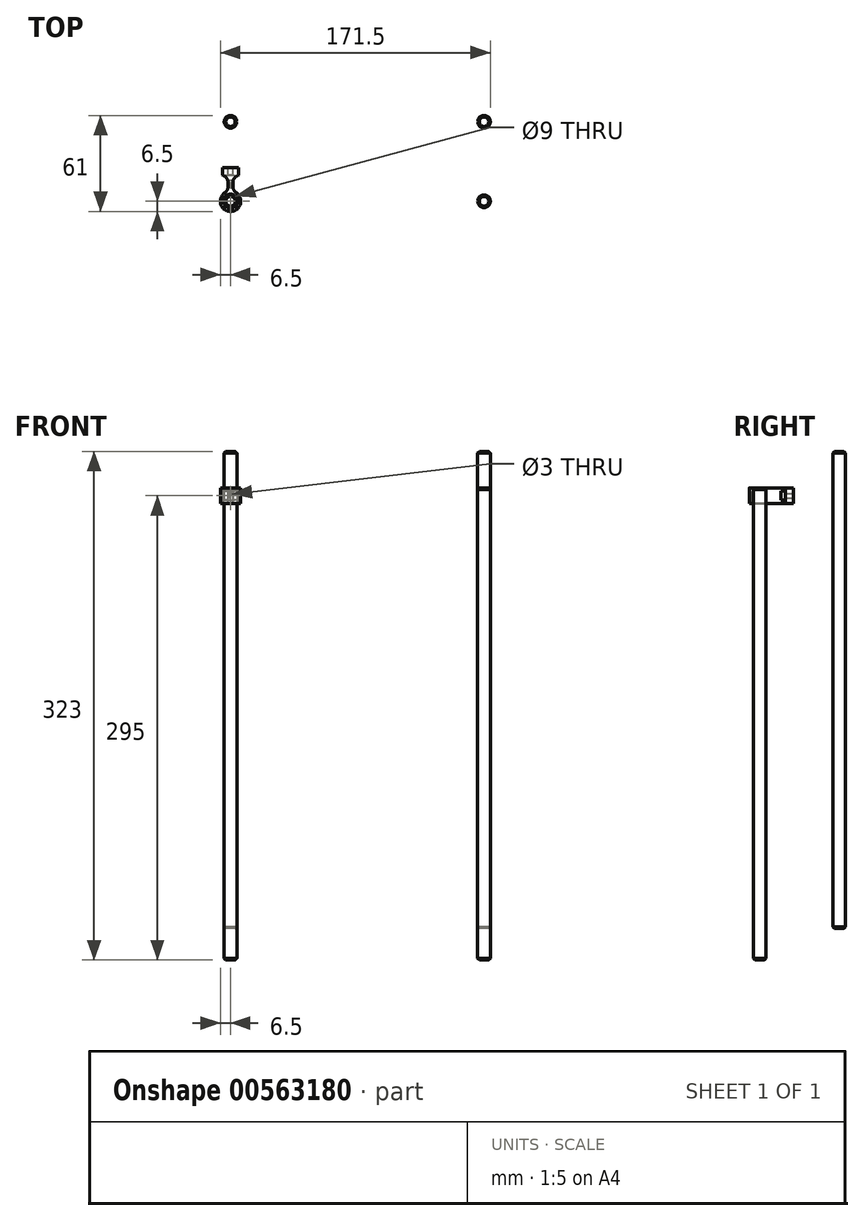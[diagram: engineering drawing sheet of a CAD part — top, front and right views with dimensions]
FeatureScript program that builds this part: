
annotation { "Feature Type Name" : "Feature", "Feature Type Description" : "" }
export const myFeature = defineFeature(function(context is Context, id is Id, definition is map)
    precondition{}
    {
        {
            var Q0;
            Q0=qCreatedBy(makeId("Top.planeOp"),FACE);
            var sketch = newSketch(context, id + "F0", { "sketchPlane" : qUnion([Q0])});
            skCircle(sketch, "E0", {"center": v(-80.5, 0) * mm, "radius": 4 * mm});
            skCircle(sketch, "E1", {"center": v(80.5, 0) * mm, "radius": 4 * mm});
            skLineSegment(sketch, "E2", {"start": v(-80.5, 0) * mm, "end": v(0, 0) * mm, "construction": true});
            skLineSegment(sketch, "E3", {"start": v(0, 0) * mm, "end": v(80.5, 0) * mm, "construction": true});
            skSolve(sketch);
        }
        {
            var Q0;
            Q0=makeQuery(id+"F0.imprint","IMPRINT",FACE,{"disambiguationData":[TD([[makeQuery(id+"F0.imprint","IMPRINT",EDGE,{"derivedFrom":sQuery(id+"F0.wireOp",EDGE,"E0")}),1.0]])]});
            var Q1;
            Q1=makeQuery(id+"F0.imprint","IMPRINT",FACE,{"disambiguationData":[TD([[makeQuery(id+"F0.imprint","IMPRINT",EDGE,{"derivedFrom":sQuery(id+"F0.wireOp",EDGE,"E1")}),1.0]])]});
            extrude(context, id + "F1", {"entities" : qUnion([Q0, Q1]), "depth" : 303 * mm, "offsetDistance" : 25 * mm});
        }
        {
            var Q0;
            Q0=makeQuery(id+"F1.opExtrude","CAP_EDGE",EDGE,{"disambiguationData":[OSD([sQuery(id+"F0.wireOp",EDGE,"E0")])],"isStart":true});
            var Q1;
            Q1=makeQuery(id+"F1.opExtrude","CAP_EDGE",EDGE,{"disambiguationData":[OSD([sQuery(id+"F0.wireOp",EDGE,"E1")])],"isStart":true});
            var Q2;
            Q2=makeQuery(id+"F1.opExtrude","CAP_EDGE",EDGE,{"disambiguationData":[OSD([sQuery(id+"F0.wireOp",EDGE,"E0")])],"isStart":false});
            var Q3;
            Q3=makeQuery(id+"F1.opExtrude","CAP_EDGE",EDGE,{"disambiguationData":[OSD([sQuery(id+"F0.wireOp",EDGE,"E1")])],"isStart":false});
            chamfer(context, id + "F2", {"entities" : qUnion([Q0, Q1, Q2, Q3]), "width" : 1 * mm, "tangentPropagation" : true});
        }
        {
            var Q0;
            Q0=qCreatedBy(makeId("Top.planeOp"),FACE);
            var sketch = newSketch(context, id + "F3", { "sketchPlane" : qUnion([Q0])});
            skLineSegment(sketch, "E4", {"start": v(0, 0) * mm, "end": v(0, -50.5) * mm, "construction": true});
            skLineSegment(sketch, "E5", {"start": v(0, -50.5) * mm, "end": v(80.5, -50.5) * mm, "construction": true});
            skLineSegment(sketch, "E6", {"start": v(0, -50.5) * mm, "end": v(-80.5, -50.5) * mm, "construction": true});
            skCircle(sketch, "E7.0", {"center": v(80.5, 0) * mm, "radius": 4 * mm});
            skLineSegment(sketch, "E8", {"start": v(80.5, 0) * mm, "end": v(80.5, -50.5) * mm, "construction": true});
            skCircle(sketch, "E9", {"center": v(-80.5, -50.5) * mm, "radius": 4 * mm});
            skCircle(sketch, "E10", {"center": v(80.5, -50.5) * mm, "radius": 4 * mm});
            skSolve(sketch);
        }
        {
            var Q0;
            Q0=makeQuery(id+"F3.imprint","IMPRINT",FACE,{"disambiguationData":[TD([[makeQuery(id+"F3.imprint","IMPRINT",EDGE,{"derivedFrom":sQuery(id+"F3.wireOp",EDGE,"E9")}),1.0]])]});
            var Q1;
            Q1=makeQuery(id+"F3.imprint","IMPRINT",FACE,{"disambiguationData":[TD([[makeQuery(id+"F3.imprint","IMPRINT",EDGE,{"derivedFrom":sQuery(id+"F3.wireOp",EDGE,"E10")}),1.0]])]});
            extrude(context, id + "F4", {"entities" : qUnion([Q0, Q1]), "depth" : 280 * mm, "offsetDistance" : 25 * mm, "hasSecondDirection" : true, "secondDirectionOppositeDirection" : true, "secondDirectionDepth" : 20 * mm});
        }
        {
            var Q0;
            Q0=makeQuery(id+"F4.opExtrude","CAP_EDGE",EDGE,{"disambiguationData":[OSD([sQuery(id+"F3.wireOp",EDGE,"E9")])],"isStart":false});
            var Q1;
            Q1=makeQuery(id+"F4.opExtrude","CAP_EDGE",EDGE,{"disambiguationData":[OSD([sQuery(id+"F3.wireOp",EDGE,"E10")])],"isStart":false});
            var Q2;
            Q2=makeQuery(id+"F4.opExtrude","CAP_EDGE",EDGE,{"disambiguationData":[OSD([sQuery(id+"F3.wireOp",EDGE,"E9")])],"isStart":true});
            var Q3;
            Q3=makeQuery(id+"F4.opExtrude","CAP_EDGE",EDGE,{"disambiguationData":[OSD([sQuery(id+"F3.wireOp",EDGE,"E10")])],"isStart":true});
            chamfer(context, id + "F5", {"entities" : qUnion([Q0, Q1, Q2, Q3]), "width" : 1 * mm, "tangentPropagation" : true});
        }
        {
            var Q0;
            Q0=makeQuery(id+"F4.opExtrude","CAP_FACE",FACE,{"disambiguationData":[OSD([sQuery(id+"F3.wireOp",EDGE,"E9")])],"isStart":false});
            var sketch = newSketch(context, id + "F6", { "sketchPlane" : qUnion([Q0])});
            skCircle(sketch, "E11", {"center": v(-80.5, -50.5) * mm, "radius": 4.5 * mm});
            skArc(sketch, "E12", {"start": v(-82, -44.18) * mm, "mid": v(-80.5, -57) * mm, "end": v(-79, -44.18) * mm});
            skLineSegment(sketch, "E13", {"start": v(-82, -44.18) * mm, "end": v(-82, -34) * mm});
            skLineSegment(sketch, "E14", {"start": v(-82, -34) * mm, "end": v(-85.5, -34) * mm});
            skLineSegment(sketch, "E15", {"start": v(-85.5, -34) * mm, "end": v(-85.5, -29) * mm});
            skLineSegment(sketch, "E16", {"start": v(-85.5, -29) * mm, "end": v(-75.5, -29) * mm});
            skLineSegment(sketch, "E17", {"start": v(-75.5, -29) * mm, "end": v(-75.5, -34) * mm});
            skLineSegment(sketch, "E18", {"start": v(-75.5, -34) * mm, "end": v(-79, -34) * mm});
            skLineSegment(sketch, "E19", {"start": v(-79, -34) * mm, "end": v(-79, -44.18) * mm});
            skLineSegment(sketch, "E20", {"start": v(-80.5, -50.5) * mm, "end": v(-80.5, -29) * mm, "construction": true});
            skSolve(sketch);
        }
        {
            var Q0;
            Q0=makeQuery(id+"F6.imprint","IMPRINT",FACE,{"disambiguationData":[TD([[makeQuery(id+"F6.imprint","IMPRINT",EDGE,{"derivedFrom":sQuery(id+"F6.wireOp",EDGE,"E11")}),-1.0]])]});
            extrude(context, id + "F7", {"entities" : qUnion([Q0]), "oppositeDirection" : true, "depth" : 10 * mm, "offsetDistance" : 25 * mm});
        }
        {
            var Q0;
            Q0=makeQuery(id+"F7.opExtrude","SWEPT_FACE",FACE,{"disambiguationData":[OSD([sQuery(id+"F6.wireOp",EDGE,"E16")])]});
            var sketch = newSketch(context, id + "F8", { "sketchPlane" : qUnion([Q0])});
            skCircle(sketch, "E21", {"center": v(80.5, 275) * mm, "radius": 1.5 * mm});
            skLineSegment(sketch, "E22", {"start": v(80.5, 275) * mm, "end": v(80.5, 270) * mm, "construction": true});
            skLineSegment(sketch, "E23", {"start": v(80.5, 275) * mm, "end": v(75.5, 275) * mm, "construction": true});
            skSolve(sketch);
        }
        {
            var Q0;
            Q0=makeQuery(id+"F7.opExtrude","SWEPT_FACE",FACE,{"disambiguationData":[OSD([sQuery(id+"F6.wireOp",EDGE,"E19")])]});
            var sketch = newSketch(context, id + "F9", { "sketchPlane" : qUnion([Q0])});
            skLineSegment(sketch, "E24.bottom", {"start": v(-34, 277.85) * mm, "end": v(-37, 277.85) * mm});
            skLineSegment(sketch, "E24.top", {"start": v(-34, 272.15) * mm, "end": v(-37, 272.15) * mm});
            skLineSegment(sketch, "E24.left", {"start": v(-34, 277.85) * mm, "end": v(-34, 272.15) * mm});
            skLineSegment(sketch, "E24.right", {"start": v(-37, 277.85) * mm, "end": v(-37, 272.15) * mm});
            skPoint(sketch, "E25", {"position": v(-34, 275) * mm});
            skLineSegment(sketch, "E26", {"start": v(-37, 275) * mm, "end": v(-34, 275) * mm, "construction": true});
            skSolve(sketch);
        }
        {
            var Q0;
            Q0=makeQuery(id+"F9.imprint","IMPRINT",FACE,{"disambiguationData":[TD([[makeQuery(id+"F9.imprint","IMPRINT",EDGE,{"derivedFrom":sQuery(id+"F9.wireOp",EDGE,"E24.bottom")}),1.0]])]});
            var Q1;
            Q1=makeQuery(id+"F7.opExtrude","SWEPT_FACE",FACE,{"disambiguationData":[OSD([sQuery(id+"F6.wireOp",EDGE,"E13")])]});
            extrude(context, id + "F10", {"entities" : qUnion([Q0]), "operationType" : NewBodyOperationType.REMOVE, "endBound" : BoundingType.UP_TO_SURFACE, "oppositeDirection" : true, "depth" : 25 * mm, "endBoundEntityFace" : qUnion([Q1]), "offsetDistance" : 25 * mm});
        }
        {
            var Q0;
            Q0=makeQuery(id+"F8.imprint","IMPRINT",FACE,{"disambiguationData":[TD([[makeQuery(id+"F8.imprint","IMPRINT",EDGE,{"derivedFrom":sQuery(id+"F8.wireOp",EDGE,"E21")}),1.0]])]});
            extrude(context, id + "F11", {"entities" : qUnion([Q0]), "operationType" : NewBodyOperationType.REMOVE, "oppositeDirection" : true, "depth" : 7 * mm, "offsetDistance" : 25 * mm});
        }
        {
            var Q0;
            {var subQ0=sQuery(id+"F6.wireOp",EDGE,"E18");var subQ1=sQuery(id+"F6.wireOp",EDGE,"E19");Q0=makeQuery(id+"F10.boolean.opBoolean","SPLIT",EDGE,{"disambiguationData":[TD([makeQuery(id+"F10.opExtrude","SWEPT_FACE",FACE,{"disambiguationData":[OSD([sQuery(id+"F9.wireOp",EDGE,"E24.bottom")])]})])],"derivedFrom":makeQuery(id+"F7.opExtrude","SWEPT_EDGE",EDGE,{"disambiguationData":[OSD([subQ0,subQ1])]})});}
            var Q1;
            {var subQ0=sQuery(id+"F6.wireOp",EDGE,"E14");var subQ2=sQuery(id+"F6.wireOp",EDGE,"E13");Q1=makeQuery(id+"F10.boolean.opBoolean","SPLIT",EDGE,{"disambiguationData":[TD([makeQuery(id+"F10.opExtrude","SWEPT_FACE",FACE,{"disambiguationData":[OSD([sQuery(id+"F9.wireOp",EDGE,"E24.bottom")])]})])],"derivedFrom":makeQuery(id+"F7.opExtrude","SWEPT_EDGE",EDGE,{"disambiguationData":[OSD([subQ2,subQ0])]})});}
            var Q2;
            Q2=makeQuery(id+"F7.opExtrude","SWEPT_EDGE",EDGE,{"disambiguationData":[OSD([sQuery(id+"F6.wireOp",EDGE,"E12"),sQuery(id+"F6.wireOp",EDGE,"E19")])]});
            var Q3;
            Q3=makeQuery(id+"F7.opExtrude","SWEPT_EDGE",EDGE,{"disambiguationData":[OSD([sQuery(id+"F6.wireOp",EDGE,"E12"),sQuery(id+"F6.wireOp",EDGE,"E13")])]});
            fillet(context, id + "F12", {"entities" : qUnion([Q0, Q1, Q2, Q3]), "tangentPropagation" : true, "radius" : 5 * mm, "defaultsChanged" : false, "vertexSettings" : [], "allowEdgeOverflow" : false});
        }
    });
